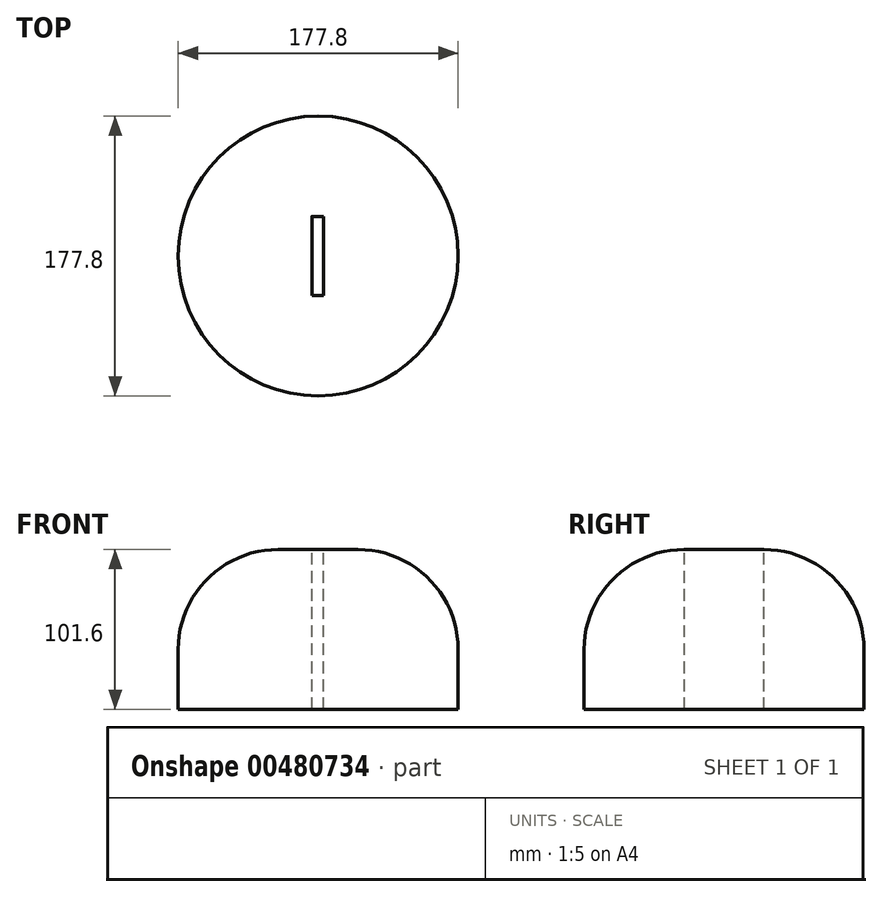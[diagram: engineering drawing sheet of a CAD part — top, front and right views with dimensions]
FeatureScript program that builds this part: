
annotation { "Feature Type Name" : "Feature", "Feature Type Description" : "" }
export const myFeature = defineFeature(function(context is Context, id is Id, definition is map)
    precondition{}
    {
        {
            var Q0;
            Q0=qCreatedBy(makeId("Top.planeOp"),FACE);
            var sketch = newSketch(context, id + "F0", { "sketchPlane" : qUnion([Q0])});
            skCircle(sketch, "E0", {"center": v(0, 0) * mm, "radius": 88.9 * mm});
            skSolve(sketch);
        }
        {
            var Q0;
            Q0=qSketchRegion(id+"F0",true);
            extrude(context, id + "F1", {"entities" : qUnion([Q0]), "depth" : 101.6 * mm});
        }
        {
            var Q0;
            Q0=makeQuery(id+"F1.opExtrude","CAP_EDGE",EDGE,{"disambiguationData":[OSD([sQuery(id+"F0.wireOp",EDGE,"E0")])],"isStart":false});
            fillet(context, id + "F2", {"entities" : qUnion([Q0]), "radius" : 63.5 * mm, "tangentPropagation" : true, "allowEdgeOverflow" : false});
        }
        {
            var Q0;
            Q0=makeQuery(id+"F1.opExtrude","CAP_FACE",FACE,{"disambiguationData":[OSD([sQuery(id+"F0.wireOp",EDGE,"E0")])],"isStart":false});
            var sketch = newSketch(context, id + "F3", { "sketchPlane" : qUnion([Q0])});
            skLineSegment(sketch, "E1.bottom", {"start": v(3.28, 25.19) * mm, "end": v(-4.05, 25.19) * mm});
            skLineSegment(sketch, "E1.top", {"start": v(3.28, -25.08) * mm, "end": v(-4.05, -25.08) * mm});
            skLineSegment(sketch, "E1.left", {"start": v(3.28, 25.19) * mm, "end": v(3.28, -25.08) * mm});
            skLineSegment(sketch, "E1.right", {"start": v(-4.05, 25.19) * mm, "end": v(-4.05, -25.08) * mm});
            skSolve(sketch);
        }
        {
            var Q0;
            Q0=qSketchRegion(id+"F3",true);
            extrude(context, id + "F4", {"entities" : qUnion([Q0]), "operationType" : NewBodyOperationType.REMOVE, "oppositeDirection" : true, "depth" : 101.6 * mm});
        }
    });
